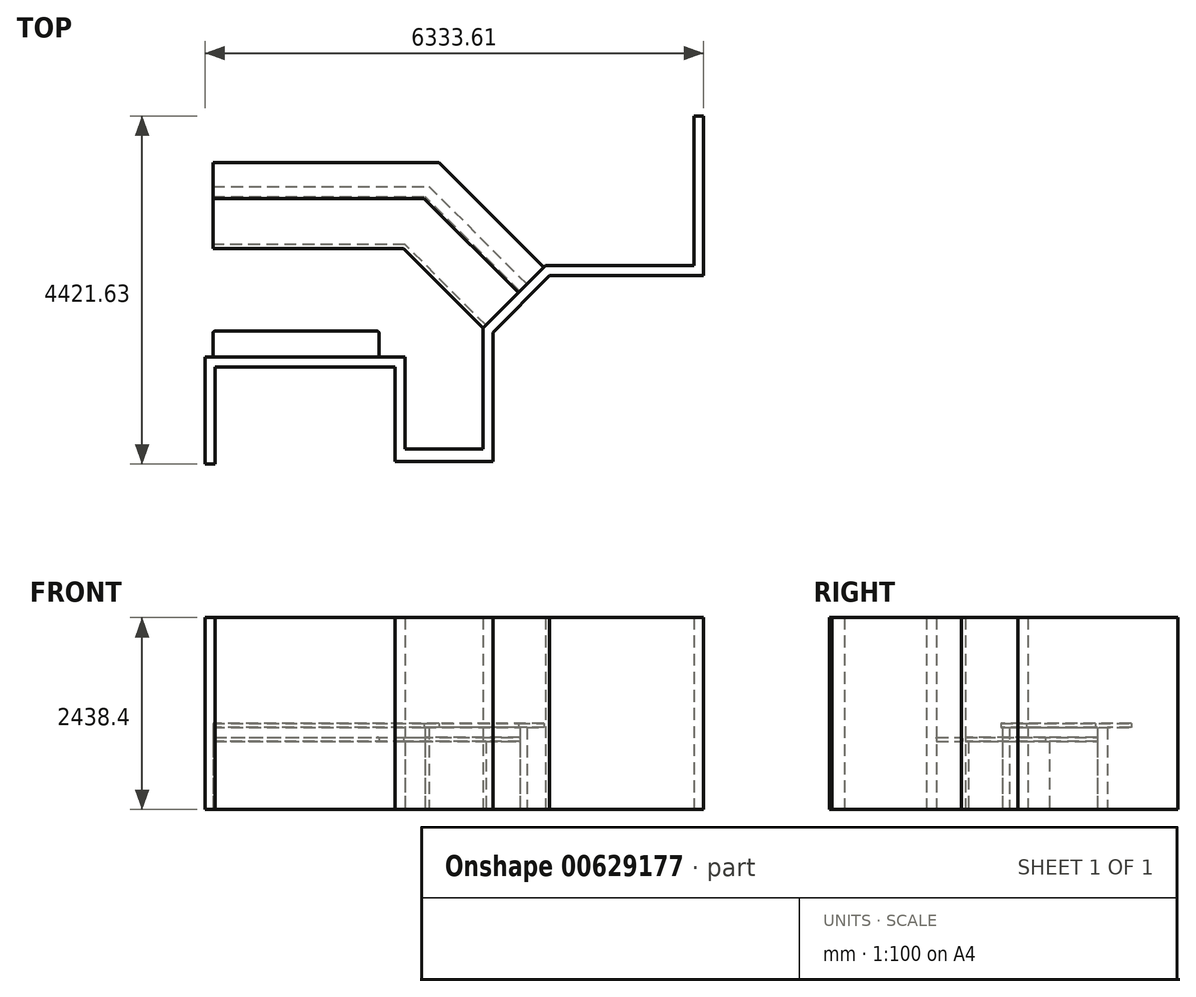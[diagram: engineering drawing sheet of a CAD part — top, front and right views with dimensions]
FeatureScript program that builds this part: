
annotation { "Feature Type Name" : "Feature", "Feature Type Description" : "" }
export const myFeature = defineFeature(function(context is Context, id is Id, definition is map)
    precondition{}
    {
        {
            var Q0;
            Q0=qCreatedBy(makeId("Top.planeOp"),FACE);
            var sketch = newSketch(context, id + "F0", { "sketchPlane" : qUnion([Q0])});
            skLineSegment(sketch, "E0", {"start": v(-1243.02, 0) * mm, "end": v(1296.98, 0) * mm});
            skLineSegment(sketch, "E1", {"start": v(1296.98, 0) * mm, "end": v(1296.98, -1168.4) * mm});
            skLineSegment(sketch, "E2", {"start": v(1296.98, -1168.4) * mm, "end": v(2287.58, -1168.4) * mm});
            skLineSegment(sketch, "E3", {"start": v(2287.58, -1168.4) * mm, "end": v(2287.58, 368.3) * mm});
            skLineSegment(sketch, "E4", {"start": v(2287.58, 368.3) * mm, "end": v(3082.33, 1163.05) * mm});
            skLineSegment(sketch, "E5", {"start": v(3082.33, 1163.05) * mm, "end": v(4967.08, 1163.05) * mm});
            skLineSegment(sketch, "E6", {"start": v(4967.08, 3063.83) * mm, "end": v(4967.08, 1163.05) * mm});
            skLineSegment(sketch, "E7", {"start": v(-1243.02, 0) * mm, "end": v(-1243.02, -1357.8) * mm});
            skLineSegment(sketch, "E8.bottom", {"start": v(-1116.02, 0) * mm, "end": v(941.38, 0) * mm});
            skLineSegment(sketch, "E8.top", {"start": v(-1116.02, 304.8) * mm, "end": v(941.38, 304.8) * mm});
            skLineSegment(sketch, "E8.left", {"start": v(-1116.02, 0) * mm, "end": v(-1116.02, 304.8) * mm});
            skLineSegment(sketch, "E8.right", {"start": v(941.38, 0) * mm, "end": v(941.38, 304.8) * mm});
            skLineSegment(sketch, "E9", {"start": v(2324.68, 405.4) * mm, "end": v(1296.98, 1433.1) * mm});
            skLineSegment(sketch, "E10", {"start": v(2755.73, 836.45) * mm, "end": v(1549.48, 2042.7) * mm});
            skLineSegment(sketch, "E11", {"start": v(1296.98, 0) * mm, "end": v(1296.98, 1433.1) * mm, "construction": true});
            skLineSegment(sketch, "E12", {"start": v(1296.98, 1433.1) * mm, "end": v(-1141.42, 1433.1) * mm});
            skLineSegment(sketch, "E13", {"start": v(-1141.42, 2042.7) * mm, "end": v(-1141.42, 1433.1) * mm});
            skLineSegment(sketch, "E14", {"start": v(-1141.42, 2042.7) * mm, "end": v(1549.48, 2042.7) * mm});
            skLineSegment(sketch, "E15", {"start": v(2845.53, 926.25) * mm, "end": v(1602.09, 2169.7) * mm});
            skLineSegment(sketch, "E16", {"start": v(-1141.42, 2169.7) * mm, "end": v(1602.09, 2169.7) * mm});
            skLineSegment(sketch, "E17", {"start": v(-1141.42, 2169.7) * mm, "end": v(-1141.42, 2042.7) * mm});
            skLineSegment(sketch, "E18", {"start": v(3061.06, 1141.78) * mm, "end": v(1728.34, 2474.5) * mm});
            skLineSegment(sketch, "E19", {"start": v(1728.34, 2474.5) * mm, "end": v(-1141.42, 2474.5) * mm});
            skLineSegment(sketch, "E20", {"start": v(-1141.42, 2474.5) * mm, "end": v(-1141.42, 2169.7) * mm});
            skLineSegment(sketch, "E21", {"start": v(4967.08, 3063.83) * mm, "end": v(5090.59, 3063.83) * mm});
            skLineSegment(sketch, "E22", {"start": v(5090.59, 3063.83) * mm, "end": v(5090.59, 1036.05) * mm});
            skLineSegment(sketch, "E23", {"start": v(5090.59, 1036.05) * mm, "end": v(3134.94, 1036.05) * mm});
            skLineSegment(sketch, "E24", {"start": v(3134.94, 1036.05) * mm, "end": v(2414.58, 315.7) * mm});
            skLineSegment(sketch, "E25", {"start": v(2414.58, 315.7) * mm, "end": v(2414.58, -1328.1) * mm});
            skLineSegment(sketch, "E26", {"start": v(2414.58, -1328.1) * mm, "end": v(1169.98, -1328.1) * mm});
            skLineSegment(sketch, "E27", {"start": v(1169.98, -1328.1) * mm, "end": v(1169.98, -127) * mm});
            skLineSegment(sketch, "E28", {"start": v(1169.98, -127) * mm, "end": v(-1116.02, -127) * mm});
            skLineSegment(sketch, "E29", {"start": v(-1116.02, -127) * mm, "end": v(-1116.02, -1357.8) * mm});
            skLineSegment(sketch, "E30", {"start": v(-1116.02, -1357.8) * mm, "end": v(-1243.02, -1357.8) * mm});
            skSolve(sketch);
        }
        {
            var Q0;
            {var subQ1=sQuery(id+"F0.wireOp",EDGE,"E9");Q0=makeQuery(id+"F0.imprint","IMPRINT",FACE,{"disambiguationData":[TD([[makeQuery(id+"F0.imprint","IMPRINT",EDGE,{"derivedFrom":subQ1}),-1.0]])]});}
            var Q1;
            Q1=makeQuery(id+"F0.imprint","IMPRINT",FACE,{"disambiguationData":[TD([[makeQuery(id+"F0.imprint","IMPRINT",EDGE,{"derivedFrom":sQuery(id+"F0.wireOp",EDGE,"E8.bottom")}),1.0]])]});
            extrude(context, id + "F1", {"entities" : qUnion([Q0, Q1]), "depth" : 863.6 * mm, "offsetDistance" : 25.4 * mm});
        }
        {
            var Q0;
            {var subQ3=sQuery(id+"F0.wireOp",EDGE,"E1");Q0=makeQuery(id+"F0.imprint","IMPRINT",FACE,{"disambiguationData":[TD([[makeQuery(id+"F0.imprint","IMPRINT",EDGE,{"derivedFrom":subQ3}),-1.0]])]});}
            extrude(context, id + "F2", {"entities" : qUnion([Q0]), "depth" : 2438.4 * mm, "offsetDistance" : 25.4 * mm});
        }
        {
            var Q0;
            {var subQ0=sQuery(id+"F0.wireOp",EDGE,"E10");Q0=makeQuery(id+"F0.imprint","IMPRINT",FACE,{"disambiguationData":[TD([[makeQuery(id+"F0.imprint","IMPRINT",EDGE,{"derivedFrom":subQ0}),-1.0]])]});}
            extrude(context, id + "F3", {"entities" : qUnion([Q0]), "depth" : 1041.4 * mm, "offsetDistance" : 25.4 * mm});
        }
        {
            var Q0;
            Q0=makeQuery(id+"F3.opExtrude","CAP_FACE",FACE,{"disambiguationData":[OSD([sQuery(id+"F0.wireOp",EDGE,"E4"),sQuery(id+"F0.wireOp",EDGE,"E10"),sQuery(id+"F0.wireOp",EDGE,"E14"),sQuery(id+"F0.wireOp",EDGE,"E15"),sQuery(id+"F0.wireOp",EDGE,"E16"),sQuery(id+"F0.wireOp",EDGE,"E17")])],"isStart":false});
            var sketch = newSketch(context, id + "F4", { "sketchPlane" : qUnion([Q0])});
            skLineSegment(sketch, "E31", {"start": v(2737.77, 818.5) * mm, "end": v(3061.06, 1141.78) * mm});
            skLineSegment(sketch, "E32", {"start": v(3061.06, 1141.78) * mm, "end": v(1728.34, 2474.5) * mm});
            skLineSegment(sketch, "E33", {"start": v(1728.34, 2474.5) * mm, "end": v(-1141.42, 2474.5) * mm});
            skLineSegment(sketch, "E34", {"start": v(-1141.42, 2474.5) * mm, "end": v(-1141.42, 2017.3) * mm});
            skLineSegment(sketch, "E35", {"start": v(-1141.42, 2017.3) * mm, "end": v(1538.96, 2017.3) * mm});
            skLineSegment(sketch, "E36", {"start": v(1538.96, 2017.3) * mm, "end": v(2737.77, 818.5) * mm});
            skSolve(sketch);
        }
        {
            var Q0;
            Q0=qSketchRegion(id+"F4",true);
            extrude(context, id + "F5", {"entities" : qUnion([Q0]), "operationType" : NewBodyOperationType.ADD, "depth" : 50.8 * mm, "offsetDistance" : 25.4 * mm});
        }
        {
            var Q0;
            Q0=makeQuery(id+"F1.opExtrude","CAP_FACE",FACE,{"disambiguationData":[OSD([sQuery(id+"F0.wireOp",EDGE,"E4"),sQuery(id+"F0.wireOp",EDGE,"E9"),sQuery(id+"F0.wireOp",EDGE,"E10"),sQuery(id+"F0.wireOp",EDGE,"E12"),sQuery(id+"F0.wireOp",EDGE,"E13"),sQuery(id+"F0.wireOp",EDGE,"E14")])],"isStart":false});
            var sketch = newSketch(context, id + "F6", { "sketchPlane" : qUnion([Q0])});
            skLineSegment(sketch, "E37", {"start": v(2755.73, 836.45) * mm, "end": v(1549.48, 2042.7) * mm});
            skLineSegment(sketch, "E38", {"start": v(1549.48, 2042.7) * mm, "end": v(-1141.42, 2042.7) * mm});
            skLineSegment(sketch, "E39", {"start": v(-1141.42, 2042.7) * mm, "end": v(-1141.42, 1382.3) * mm});
            skLineSegment(sketch, "E40", {"start": v(-1141.42, 1382.3) * mm, "end": v(1275.94, 1382.3) * mm});
            skLineSegment(sketch, "E41", {"start": v(1275.94, 1382.3) * mm, "end": v(2288.76, 369.48) * mm});
            skLineSegment(sketch, "E42", {"start": v(2755.73, 836.45) * mm, "end": v(2288.76, 369.48) * mm});
            skLineSegment(sketch, "E43.bottom", {"start": v(-1141.42, 0) * mm, "end": v(966.78, 0) * mm});
            skLineSegment(sketch, "E43.top", {"start": v(-1141.42, 330.2) * mm, "end": v(966.78, 330.2) * mm});
            skLineSegment(sketch, "E43.left", {"start": v(-1141.42, 0) * mm, "end": v(-1141.42, 330.2) * mm});
            skLineSegment(sketch, "E43.right", {"start": v(966.78, 0) * mm, "end": v(966.78, 330.2) * mm});
            skSolve(sketch);
        }
        {
            var Q0;
            Q0=makeQuery(id+"F6.imprint","IMPRINT",FACE,{"disambiguationData":[TD([[makeQuery(id+"F6.imprint","IMPRINT",EDGE,{"derivedFrom":sQuery(id+"F6.wireOp",EDGE,"E43.bottom")}),1.0]])]});
            var Q1;
            {var subQ2=sQuery(id+"F6.wireOp",EDGE,"E37");Q1=makeQuery(id+"F6.imprint","IMPRINT",FACE,{"disambiguationData":[TD([[makeQuery(id+"F6.imprint","IMPRINT",EDGE,{"derivedFrom":subQ2}),1.0]])]});}
            var Q2;
            {var subQ3=sQuery(id+"F6.wireOp",EDGE,"E40");Q2=makeQuery(id+"F6.imprint","IMPRINT",FACE,{"disambiguationData":[TD([[makeQuery(id+"F6.imprint","IMPRINT",EDGE,{"derivedFrom":subQ3}),1.0]])]});}
            var Q3;
            Q3=sQuery(id+"F6.wireOp",EDGE,"E43.left");
            var Q4;
            Q4=sQuery(id+"F6.wireOp",EDGE,"E41");
            var Q5;
            Q5=sQuery(id+"F6.wireOp",EDGE,"E43.top");
            var Q6;
            Q6=sQuery(id+"F6.wireOp",EDGE,"E43.right");
            var Q7;
            Q7=sQuery(id+"F6.wireOp",EDGE,"E40");
            var Q8;
            Q8=sQuery(id+"F6.wireOp",EDGE,"E39");
            extrude(context, id + "F7", {"entities" : qUnion([Q0, Q1, Q2]), "surfaceEntities" : qUnion([Q3, Q4, Q5, Q6, Q7, Q8]), "depth" : 50.8 * mm, "offsetDistance" : 25.4 * mm});
        }
        {
            var Q0;
            Q0=makeQuery(id+"F7.opExtrude","SWEPT_EDGE",EDGE,{"disambiguationData":[OSD([sQuery(id+"F6.wireOp",EDGE,"E43.top"),sQuery(id+"F6.wireOp",EDGE,"E43.left")])]});
            var Q1;
            Q1=makeQuery(id+"F7.opExtrude","SWEPT_EDGE",EDGE,{"disambiguationData":[OSD([sQuery(id+"F6.wireOp",EDGE,"E43.top"),sQuery(id+"F6.wireOp",EDGE,"E43.right")])]});
            fillet(context, id + "F8", {"entities" : qUnion([Q0, Q1]), "radius" : 25.4 * mm, "tangentPropagation" : true, "allowEdgeOverflow" : false});
        }
        {
            var Q0;
            Q0=makeQuery(id+"F7.opExtrude","CAP_EDGE",EDGE,{"disambiguationData":[OSD([sQuery(id+"F6.wireOp",EDGE,"E43.right")])],"isStart":false});
            var Q1;
            Q1=makeQuery(id+"F7.opExtrude","CAP_EDGE",EDGE,{"disambiguationData":[OSD([sQuery(id+"F6.wireOp",EDGE,"E43.top")])],"isStart":false});
            fillet(context, id + "F9", {"entities" : qUnion([Q0, Q1]), "radius" : 12.7 * mm, "tangentPropagation" : true, "allowEdgeOverflow" : false});
        }
    });
